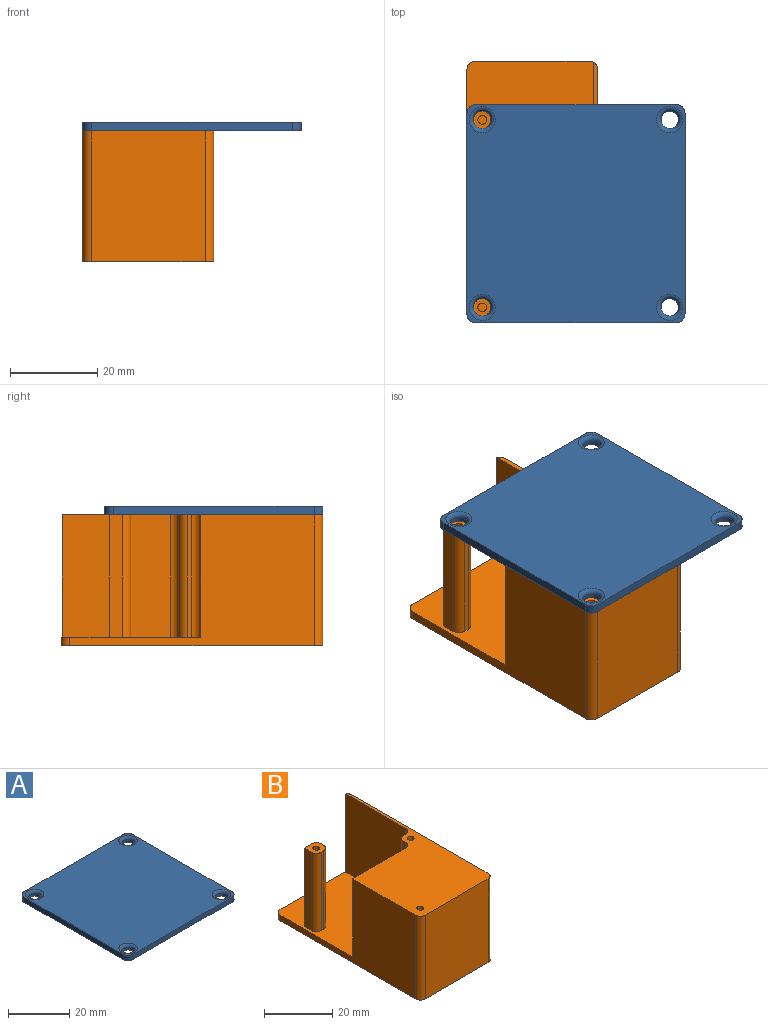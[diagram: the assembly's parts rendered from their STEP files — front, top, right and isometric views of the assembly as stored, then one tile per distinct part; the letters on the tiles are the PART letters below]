
ASSEMBLY  parts=2 mates=1
PART A: 18 faces, bbox 50x50x2 mm
  f0: plane 46x2mm, normal (0,1,0), area 92mm2, adj f4,f5,f14,f17
  f1: plane 46x2mm, normal (-1,0,0), area 92mm2, adj f4,f5,f14,f15
  f2: plane 46x2mm, normal (0,-1,0), area 92mm2, adj f4,f5,f15,f16
  f3: plane 46x2mm, normal (1,0,0), area 92mm2, adj f4,f5,f16,f17
  f4: plane 50x50mm, normal (0,0,1), area 2383.5mm2, adj f0,f1,f2,f3,f10,f11,f12,f13
  f5: plane 50x50mm, normal (0,0,-1), area 2446.3mm2, adj f0,f1,f2,f3,f6,f7,f8,f9
  f6: cylinder r=2mm len=4mm, axis (0,0,1), area 12.6mm2, adj f5,f13
  f7: cylinder r=2mm len=4mm, axis (0,0,1), area 12.6mm2, adj f5,f12
  f8: cylinder r=2mm len=4mm, axis (0,0,1), area 12.6mm2, adj f5,f11
  f9: cylinder r=2mm len=4mm, axis (0,0,1), area 12.6mm2, adj f5,f10
  f10: torus R=3mm, axis (0,0,1), area 23.3mm2, adj f4,f9
  f11: torus R=3mm, axis (0,0,1), area 23.3mm2, adj f4,f8
  f12: torus R=3mm, axis (0,0,1), area 23.3mm2, adj f4,f7
  f13: torus R=3mm, axis (0,0,1), area 23.3mm2, adj f4,f6
  f14: cylinder r=2mm len=2mm, axis (0,0,1), area 6.3mm2, adj f0,f1,f4,f5
  f15: cylinder r=2mm len=2mm, axis (0,0,-1), area 6.3mm2, adj f1,f2,f4,f5
  f16: cylinder r=2mm len=2mm, axis (0,0,1), area 6.3mm2, adj f2,f3,f4,f5
  f17: cylinder r=2mm len=2mm, axis (0,0,-1), area 6.3mm2, adj f0,f3,f4,f5
PART B: 32 faces, bbox 30x60x30 mm
  f0: plane 32x29mm, normal (0,0,1), area 878.8mm2, adj f1,f2,f7,f8,f9,f10,f11,f12
  f1: plane 26x2mm, normal (0,1,0), area 52mm2, adj f0,f6,f28,f31
  f2: plane 56x30mm, normal (-1,0,0), area 840mm2, adj f0,f5,f6,f7,f28,f29
  f3: plane 30x26mm, normal (0,-1,0), area 780mm2, adj f5,f6,f29,f30
  f4: plane 56x30mm, normal (1,0,0), area 1680mm2, adj f5,f6,f30,f31
  f5: plane 59.73x30mm, normal (0,0,1), area 889.1mm2, adj f2,f3,f4,f7,f8,f14,f15,f18
  f6: plane 60x30mm, normal (0,0,-1), area 1796.6mm2, adj f1,f2,f3,f4,f28,f29,f30,f31
  f7: plane 28x22mm, normal (0,1,0), area 616mm2, adj f0,f2,f5,f24
  f8: plane 28x24.73mm, normal (-1,0,0), area 692.5mm2, adj f0,f5,f22,f31
  f9: plane 28x3mm, normal (0,1,0), area 84mm2, adj f0,f10,f13,f25
  f10: plane 28x3mm, normal (-1,0,0), area 84mm2, adj f0,f9,f13,f27
  f11: plane 28x1mm, normal (0,-1,0), area 28mm2, adj f0,f13,f26,f27
  f12: plane 28x1mm, normal (1,0,0), area 28mm2, adj f0,f13,f25,f26
  f13: plane 5x5mm, normal (0,0,1), area 19.3mm2, adj f9,f10,f11,f12,f16,f25,f26,f27
  f14: plane 28x1mm, normal (0,1,0), area 28mm2, adj f0,f5,f22,f23
  f15: plane 28x1mm, normal (-1,0,0), area 28mm2, adj f0,f5,f23,f24
  f16: cylinder r=1mm len=15mm, axis (0,0,1), area 94.2mm2, adj f13,f17
  f17: plane 2x2mm, normal (0,0,1), area 3.1mm2, adj f16
  f18: cylinder r=1mm len=15mm, axis (0,0,1), area 94.2mm2, adj f5,f19
  f19: plane 2x2mm, normal (0,0,1), area 3.1mm2, adj f18
  f20: cylinder r=1mm len=15mm, axis (0,0,1), area 94.2mm2, adj f5,f21
  f21: plane 2x2mm, normal (0,0,1), area 3.1mm2, adj f20
  f22: cylinder r=2mm len=28mm, axis (0,0,-1), area 88mm2, adj f0,f5,f8,f14
  f23: cylinder r=2mm len=28mm, axis (0,0,1), area 88mm2, adj f0,f5,f14,f15
  f24: cylinder r=2mm len=28mm, axis (0,0,-1), area 88mm2, adj f0,f5,f7,f15
  f25: cylinder r=2mm len=28mm, axis (0,0,-1), area 88mm2, adj f0,f9,f12,f13
  f26: cylinder r=2mm len=28mm, axis (0,0,1), area 88mm2, adj f0,f11,f12,f13
  f27: cylinder r=2mm len=28mm, axis (0,0,-1), area 88mm2, adj f0,f10,f11,f13
  f28: cylinder r=2mm len=2mm, axis (0,0,1), area 6.3mm2, adj f0,f1,f2,f6
  f29: cylinder r=2mm len=30mm, axis (0,0,-1), area 94.2mm2, adj f2,f3,f5,f6
  f30: cylinder r=2mm len=30mm, axis (0,0,1), area 94.2mm2, adj f3,f4,f5,f6
  f31: cylinder r=2mm len=30mm, axis (0,0,-1), area 64.9mm2, adj f0,f1,f4,f5,f6,f8
PLACE A t=(-6.07,68.27,8.8)mm
PLACE B t=(-6.11,-5.83,-21.2)mm fixed
MATE slider B.f18 <-> A.f9  axis (0,0,1) through (12.1,15.3,8.8)mm
